# Revit family: PLAFODO
name_source: partatom
category: Luminaires
units: mm (PartAtom-declared; Revit-internal decimal feet)

## family parameters
Cote de connecteur circulaire = Utiliser le diamètre
Couper avec des vides une fois chargée = Oui
Hôte = Face
Numéro OmniClass = 23.80.70.11
Partagée = Oui
Point de calcul de pièce = Oui
Source d'éclairage = Oui
Titre OmniClass = Luminaries for Internal Lighting
Type d'élément = Normal

## types (2) — shared parameters
Angle de l'inclinaison = 60.00°
Coût = 100 $
Emettre la visibilité des formes dans le rendu = Non
Emettre à partir du diamètre du cercle = 610 mm
Fabricant = Résistex
Filtre de couleur = 16777215
Garantie = 5 ans
Gradation des changements de température de couleur de lampe = <Aucun>
IK = 08
IP = 54
Image du type = <Aucun>
Indice de charge = Lighting
Matériau diffuseur = PC Transparent
Modèle = Plafodo
Nombre pôles = 1
Rayon collerette = 52 mm
Tension = 230 V
URL = https://www.resistex-sa.com
h = 110 mm  [stored 0.360892 ft]
l = 140 mm
w = 140 mm
zero-valued in all types: Elévation par défaut

## per-type parameters (varying)
| type | Charge apparente | Commentaires relatifs à la puissance | Description | Fichier de distribution photométrique |
| 961731 | 25 VA | 24W | Plafonnier étanche équipé d'une LED COB, efficacité lumineuse de 108lm/W | 961731.ies |
| 961732 | 26 VA | 25W | Plafonnier étanche équipé d'une LED COB, efficacité lumineuse de 117lm/W | 961732.ies |

note: [stored X ft] marks values corroborated as IEEE doubles in the binary element streams (Revit-internal decimal feet)

## geometry (parser evidence)
native form markers: Sweep x4
no freeform markers — native parametric forms only
